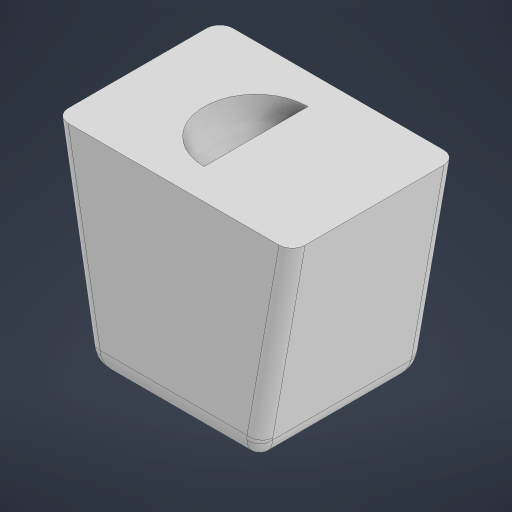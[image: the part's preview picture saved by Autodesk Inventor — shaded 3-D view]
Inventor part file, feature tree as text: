
AUTODESK INVENTOR PART (.ipt)
format: ipt  version: 2024.1 (Build 281209000, 209)  size: 558,080 bytes
history: native  units: mm
features: fillet x2, sketch x2, extrude x1, revolve x1, other x1
ambient origin geometry x8: Origin, YZ Plane, XZ Plane, XY Plane, X Axis, Y Axis, Z Axis, Center Point
bodies: Solid1 (feature_tree)
feature tree (7):
  extrude  "Extrusion1"  Depth=15.933mm
  fillet  "Fillet1"  Radius=12.64mm
  fillet  "Fillet2"  Radius=12.7mm
  revolve  "Revolution1"  [1 undecoded]
  other  "Work Axis1"
  sketch  "Sketch1"  dims[d0=2.82mm d1=15.933mm d2=12.64mm d3=12.7mm d4=0.0mm]
  sketch  "Sketch2"  dims[d5=2.0mm d6=1.0mm d7=4.0mm d8=135.0deg]
note: 1 required parameter value undecoded (feature->parameter linkage not recoverable at this tier; creation-order binding heuristic only, values carry confidence <= 0.55)
